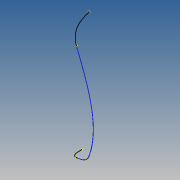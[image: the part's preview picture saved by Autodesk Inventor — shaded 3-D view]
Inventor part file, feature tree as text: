
AUTODESK INVENTOR PART (.ipt)
format: ipt  version: 2014 SP1 (Build 180222100, 222)  size: 62,976 bytes
history: native  units: mm (DEFAULTED — no unit token found)
features: other x4, plane x1, sketch x1, sweep x1
ambient origin geometry x8: Origin, YZ Plane, XZ Plane, XY Plane, X Axis, Y Axis, Z Axis, Center Point
bodies: Body1 (feature_tree)
feature tree (7):
  other  "Work Point5"
  other  "Work Point6"
  other  "Cable1:1"
  plane  "Work Plane8"
  sketch  "Sketch8"  dims[d7=0.0mm]
  other  "Srf8"
  sweep  "SweepSrf8"
